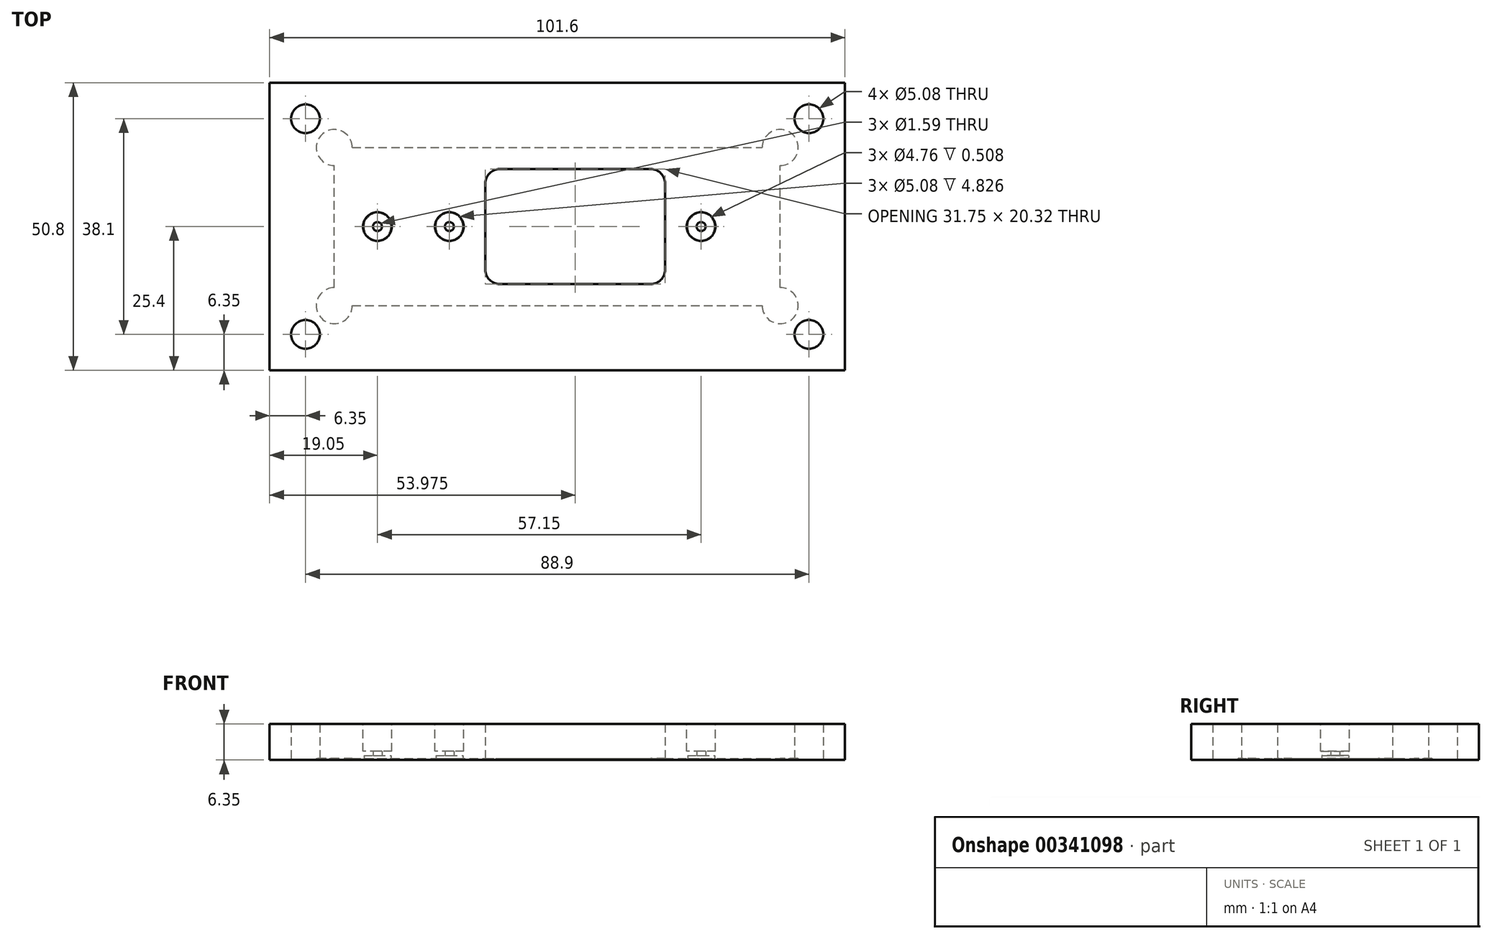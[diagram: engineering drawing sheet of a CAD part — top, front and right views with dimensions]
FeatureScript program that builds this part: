
annotation { "Feature Type Name" : "Feature", "Feature Type Description" : "" }
export const myFeature = defineFeature(function(context is Context, id is Id, definition is map)
    precondition{}
    {
        {
            var Q0;
            Q0=qCreatedBy(makeId("Top.planeOp"),FACE);
            var sketch = newSketch(context, id + "F0", { "sketchPlane" : qUnion([Q0])});
            skLineSegment(sketch, "E0.bottom", {"start": v(0, 0) * mm, "end": v(101.6, 0) * mm});
            skLineSegment(sketch, "E0.top", {"start": v(0, 50.8) * mm, "end": v(101.6, 50.8) * mm});
            skLineSegment(sketch, "E0.left", {"start": v(0, 0) * mm, "end": v(0, 50.8) * mm});
            skLineSegment(sketch, "E0.right", {"start": v(101.6, 0) * mm, "end": v(101.6, 50.8) * mm});
            skSolve(sketch);
        }
        {
            var Q0;
            Q0=makeQuery(id+"F0.imprint","IMPRINT",FACE,{"disambiguationData":[TD([[makeQuery(id+"F0.imprint","IMPRINT",EDGE,{"derivedFrom":sQuery(id+"F0.wireOp",EDGE,"E0.bottom")}),1.0]])]});
            extrude(context, id + "F1", {"entities" : qUnion([Q0]), "depth" : 6.35 * mm});
        }
        {
            var Q0;
            Q0=makeQuery(id+"F1.opExtrude","CAP_FACE",FACE,{"disambiguationData":[OSD([sQuery(id+"F0.wireOp",EDGE,"E0.bottom"),sQuery(id+"F0.wireOp",EDGE,"E0.top"),sQuery(id+"F0.wireOp",EDGE,"E0.left"),sQuery(id+"F0.wireOp",EDGE,"E0.right")])],"isStart":true});
            var sketch = newSketch(context, id + "F2", { "sketchPlane" : qUnion([Q0])});
            skLineSegment(sketch, "E1.bottom", {"start": v(11.43, -11.43) * mm, "end": v(90.17, -11.43) * mm});
            skLineSegment(sketch, "E1.top", {"start": v(11.43, -39.37) * mm, "end": v(90.17, -39.37) * mm});
            skLineSegment(sketch, "E1.left", {"start": v(11.43, -11.43) * mm, "end": v(11.43, -39.37) * mm});
            skLineSegment(sketch, "E1.right", {"start": v(90.17, -11.43) * mm, "end": v(90.17, -39.37) * mm});
            skCircle(sketch, "E2", {"center": v(11.43, -11.43) * mm, "radius": 3.18 * mm});
            skCircle(sketch, "E3", {"center": v(90.17, -11.43) * mm, "radius": 3.18 * mm});
            skCircle(sketch, "E4", {"center": v(90.17, -39.37) * mm, "radius": 3.18 * mm});
            skCircle(sketch, "E5", {"center": v(11.43, -39.37) * mm, "radius": 3.18 * mm});
            skSolve(sketch);
        }
        {
            var Q0;
            Q0=qSketchRegion(id+"F2",true);
            extrude(context, id + "F3", {"entities" : qUnion([Q0]), "operationType" : NewBodyOperationType.REMOVE, "oppositeDirection" : true, "depth" : 0.25 * mm});
        }
        {
            var Q0;
            Q0=makeQuery(id+"F1.opExtrude","CAP_FACE",FACE,{"disambiguationData":[OSD([sQuery(id+"F0.wireOp",EDGE,"E0.bottom"),sQuery(id+"F0.wireOp",EDGE,"E0.top"),sQuery(id+"F0.wireOp",EDGE,"E0.left"),sQuery(id+"F0.wireOp",EDGE,"E0.right")])],"isStart":true});
            var sketch = newSketch(context, id + "F4", { "sketchPlane" : qUnion([Q0])});
            skCircle(sketch, "E6", {"center": v(6.35, -6.35) * mm, "radius": 2.54 * mm});
            skCircle(sketch, "E7", {"center": v(95.25, -6.35) * mm, "radius": 2.54 * mm});
            skCircle(sketch, "E8", {"center": v(95.25, -44.45) * mm, "radius": 2.54 * mm});
            skCircle(sketch, "E9", {"center": v(6.35, -44.45) * mm, "radius": 2.54 * mm});
            skSolve(sketch);
        }
        {
            var Q0;
            Q0=makeQuery(id+"F4.imprint","IMPRINT",FACE,{"disambiguationData":[TD([[makeQuery(id+"F4.imprint","IMPRINT",EDGE,{"derivedFrom":sQuery(id+"F4.wireOp",EDGE,"E7")}),1.0]])]});
            var Q1;
            Q1=makeQuery(id+"F4.imprint","IMPRINT",FACE,{"disambiguationData":[TD([[makeQuery(id+"F4.imprint","IMPRINT",EDGE,{"derivedFrom":sQuery(id+"F4.wireOp",EDGE,"E6")}),1.0]])]});
            var Q2;
            Q2=makeQuery(id+"F4.imprint","IMPRINT",FACE,{"disambiguationData":[TD([[makeQuery(id+"F4.imprint","IMPRINT",EDGE,{"derivedFrom":sQuery(id+"F4.wireOp",EDGE,"E9")}),1.0]])]});
            var Q3;
            Q3=makeQuery(id+"F4.imprint","IMPRINT",FACE,{"disambiguationData":[TD([[makeQuery(id+"F4.imprint","IMPRINT",EDGE,{"derivedFrom":sQuery(id+"F4.wireOp",EDGE,"E8")}),1.0]])]});
            extrude(context, id + "F5", {"entities" : qUnion([Q0, Q1, Q2, Q3]), "operationType" : NewBodyOperationType.REMOVE, "endBound" : BoundingType.THROUGH_ALL, "oppositeDirection" : true, "depth" : 25.4 * mm});
        }
        {
            var Q0;
            Q0=makeQuery(id+"F3.boolean.opBoolean","COPY",FACE,{"derivedFrom":makeQuery(id+"F3.opExtrude","CAP_FACE",FACE,{"disambiguationData":[OSD([sQuery(id+"F2.wireOp",EDGE,"E1.bottom"),sQuery(id+"F2.wireOp",EDGE,"E1.top"),sQuery(id+"F2.wireOp",EDGE,"E1.left"),sQuery(id+"F2.wireOp",EDGE,"E1.right"),sQuery(id+"F2.wireOp",EDGE,"E2"),sQuery(id+"F2.wireOp",EDGE,"E3"),sQuery(id+"F2.wireOp",EDGE,"E4"),sQuery(id+"F2.wireOp",EDGE,"E5")])],"isStart":false})});
            var sketch = newSketch(context, id + "F6", { "sketchPlane" : qUnion([Q0])});
            skLineSegment(sketch, "E10.bottom", {"start": v(12.7, -12.7) * mm, "end": v(88.9, -12.7) * mm, "construction": true});
            skLineSegment(sketch, "E10.top", {"start": v(12.7, -38.1) * mm, "end": v(88.9, -38.1) * mm, "construction": true});
            skLineSegment(sketch, "E10.left", {"start": v(12.7, -12.7) * mm, "end": v(12.7, -38.1) * mm, "construction": true});
            skLineSegment(sketch, "E10.right", {"start": v(88.9, -12.7) * mm, "end": v(88.9, -38.1) * mm, "construction": true});
            skCircle(sketch, "E11", {"center": v(19.05, -25.4) * mm, "radius": 2.38 * mm});
            skCircle(sketch, "E12", {"center": v(31.75, -25.4) * mm, "radius": 2.38 * mm});
            skCircle(sketch, "E13", {"center": v(76.2, -25.4) * mm, "radius": 2.38 * mm});
            skSolve(sketch);
        }
        {
            var Q0;
            Q0=makeQuery(id+"F6.imprint","IMPRINT",FACE,{"disambiguationData":[TD([[makeQuery(id+"F6.imprint","IMPRINT",EDGE,{"derivedFrom":sQuery(id+"F6.wireOp",EDGE,"z2LLA9xH-Eu9N-qDuq-ZPTL-wh2qrqbxCQeN")}),1.0]])]});
            var Q1;
            Q1=makeQuery(id+"F6.imprint","IMPRINT",FACE,{"disambiguationData":[TD([[makeQuery(id+"F6.imprint","IMPRINT",EDGE,{"derivedFrom":sQuery(id+"F6.wireOp",EDGE,"E12")}),1.0]])]});
            var Q2;
            Q2=makeQuery(id+"F6.imprint","IMPRINT",FACE,{"disambiguationData":[TD([[makeQuery(id+"F6.imprint","IMPRINT",EDGE,{"derivedFrom":sQuery(id+"F6.wireOp",EDGE,"E11")}),1.0]])]});
            var Q3;
            Q3=makeQuery(id+"F6.imprint","IMPRINT",FACE,{"disambiguationData":[TD([[makeQuery(id+"F6.imprint","IMPRINT",EDGE,{"derivedFrom":sQuery(id+"F6.wireOp",EDGE,"E13")}),1.0]])]});
            extrude(context, id + "F7", {"entities" : qUnion([Q0, Q1, Q2, Q3]), "operationType" : NewBodyOperationType.REMOVE, "oppositeDirection" : true, "depth" : 0.5 * mm});
        }
        {
            var Q0;
            Q0=makeQuery(id+"F7.boolean.opBoolean","COPY",FACE,{"derivedFrom":makeQuery(id+"F7.opExtrude","CAP_FACE",FACE,{"disambiguationData":[OSD([sQuery(id+"F6.wireOp",EDGE,"E11")])],"isStart":false})});
            var sketch = newSketch(context, id + "F8", { "sketchPlane" : qUnion([Q0])});
            skCircle(sketch, "E14", {"center": v(19.05, -25.4) * mm, "radius": 0.8 * mm});
            skCircle(sketch, "E15", {"center": v(31.75, -25.4) * mm, "radius": 0.8 * mm});
            skCircle(sketch, "E16", {"center": v(76.2, -25.4) * mm, "radius": 0.8 * mm});
            skSolve(sketch);
        }
        {
            var Q0;
            Q0=qSketchRegion(id+"F8",true);
            extrude(context, id + "F9", {"entities" : qUnion([Q0]), "operationType" : NewBodyOperationType.REMOVE, "oppositeDirection" : true, "depth" : 1.27 * mm});
        }
        {
            var Q0;
            Q0=makeQuery(id+"F1.opExtrude","CAP_FACE",FACE,{"disambiguationData":[OSD([sQuery(id+"F0.wireOp",EDGE,"E0.bottom"),sQuery(id+"F0.wireOp",EDGE,"E0.top"),sQuery(id+"F0.wireOp",EDGE,"E0.left"),sQuery(id+"F0.wireOp",EDGE,"E0.right")])],"isStart":false});
            var sketch = newSketch(context, id + "F10", { "sketchPlane" : qUnion([Q0])});
            skLineSegment(sketch, "E17.bottom", {"start": v(12.7, 12.7) * mm, "end": v(88.9, 12.7) * mm, "construction": true});
            skLineSegment(sketch, "E17.top", {"start": v(12.7, 38.1) * mm, "end": v(88.9, 38.1) * mm, "construction": true});
            skLineSegment(sketch, "E17.left", {"start": v(12.7, 12.7) * mm, "end": v(12.7, 38.1) * mm, "construction": true});
            skLineSegment(sketch, "E17.right", {"start": v(88.9, 12.7) * mm, "end": v(88.9, 38.1) * mm, "construction": true});
            skCircle(sketch, "E18", {"center": v(19.05, 25.4) * mm, "radius": 2.54 * mm});
            skCircle(sketch, "E19", {"center": v(31.75, 25.4) * mm, "radius": 2.54 * mm});
            skCircle(sketch, "E20", {"center": v(76.2, 25.4) * mm, "radius": 2.54 * mm});
            skSolve(sketch);
        }
        {
            var Q0;
            Q0=qSketchRegion(id+"F10",true);
            extrude(context, id + "F11", {"entities" : qUnion([Q0]), "operationType" : NewBodyOperationType.REMOVE, "oppositeDirection" : true, "depth" : 4.83 * mm});
        }
        {
            var Q0;
            Q0=makeQuery(id+"F3.boolean.opBoolean","COPY",FACE,{"derivedFrom":makeQuery(id+"F3.opExtrude","CAP_FACE",FACE,{"disambiguationData":[OSD([sQuery(id+"F2.wireOp",EDGE,"E1.bottom"),sQuery(id+"F2.wireOp",EDGE,"E1.top"),sQuery(id+"F2.wireOp",EDGE,"E1.left"),sQuery(id+"F2.wireOp",EDGE,"E1.right"),sQuery(id+"F2.wireOp",EDGE,"E2"),sQuery(id+"F2.wireOp",EDGE,"E3"),sQuery(id+"F2.wireOp",EDGE,"E4"),sQuery(id+"F2.wireOp",EDGE,"E5")])],"isStart":false})});
            var sketch = newSketch(context, id + "F12", { "sketchPlane" : qUnion([Q0])});
            skLineSegment(sketch, "E21.bottom", {"start": v(40.64, -15.24) * mm, "end": v(67.3, -15.24) * mm});
            skLineSegment(sketch, "E21.top", {"start": v(40.64, -35.56) * mm, "end": v(67.3, -35.56) * mm});
            skLineSegment(sketch, "E21.left", {"start": v(38.1, -17.78) * mm, "end": v(38.1, -33.02) * mm});
            skLineSegment(sketch, "E21.right", {"start": v(69.85, -17.78) * mm, "end": v(69.85, -33.02) * mm});
            skPoint(sketch, "E22.visualSharp", {"position": v(38.1, -15.24) * mm});
            skArc(sketch, "E22.filletArc", {"start": v(40.64, -15.24) * mm, "mid": v(38.84, -15.98) * mm, "end": v(38.1, -17.78) * mm});
            skPoint(sketch, "E23.visualSharp", {"position": v(69.85, -15.24) * mm});
            skArc(sketch, "E23.filletArc", {"start": v(69.85, -17.78) * mm, "mid": v(69.1, -15.98) * mm, "end": v(67.3, -15.24) * mm});
            skPoint(sketch, "E24.visualSharp", {"position": v(69.85, -35.56) * mm});
            skArc(sketch, "E24.filletArc", {"start": v(67.3, -35.56) * mm, "mid": v(69.1, -34.82) * mm, "end": v(69.85, -33.02) * mm});
            skPoint(sketch, "E25.visualSharp", {"position": v(38.1, -35.56) * mm});
            skArc(sketch, "E25.filletArc", {"start": v(38.1, -33.02) * mm, "mid": v(38.84, -34.82) * mm, "end": v(40.64, -35.56) * mm});
            skSolve(sketch);
        }
        {
            var Q0;
            Q0=qSketchRegion(id+"F12",true);
            extrude(context, id + "F13", {"entities" : qUnion([Q0]), "operationType" : NewBodyOperationType.REMOVE, "endBound" : BoundingType.UP_TO_NEXT, "oppositeDirection" : true, "depth" : 25.4 * mm});
        }
    });
